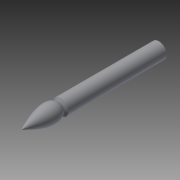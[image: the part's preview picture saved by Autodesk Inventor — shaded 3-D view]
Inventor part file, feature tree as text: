
AUTODESK INVENTOR PART (.ipt)
format: ipt  version: 2013 SP2 (Build 170200200, 200)  size: 94,208 bytes
history: native  units: mm
features: revolve x1, sketch x1
ambient origin geometry x8: Origin, YZ Plane, XZ Plane, XY Plane, X Axis, Y Axis, Z Axis, Center Point
bodies: Solid1 (feature_tree)
feature tree (2):
  revolve  "Revolution1"  [1 undecoded]
  sketch  "Sketch1"  dims[d2=8.0mm d3=50.0mm d4=20.0mm d5=90.0deg]
note: 1 required parameter value undecoded (feature->parameter linkage not recoverable at this tier; creation-order binding heuristic only, values carry confidence <= 0.55)
